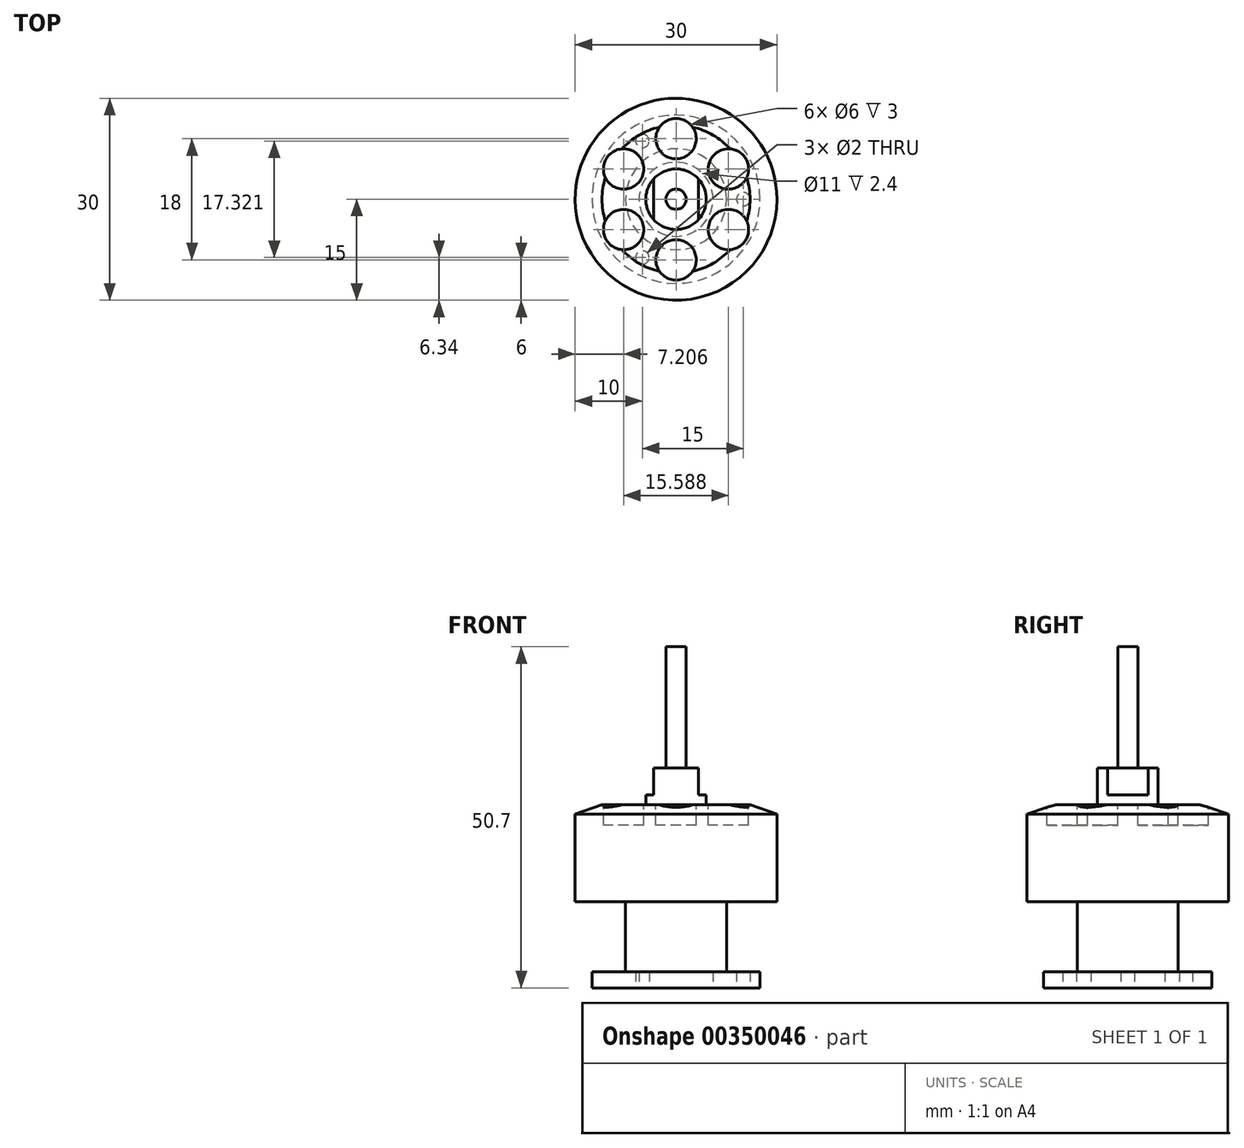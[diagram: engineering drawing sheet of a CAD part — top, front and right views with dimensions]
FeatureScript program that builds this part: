
annotation { "Feature Type Name" : "Feature", "Feature Type Description" : "" }
export const myFeature = defineFeature(function(context is Context, id is Id, definition is map)
    precondition{}
    {
        {
            var Q0;
            Q0=qCreatedBy(makeId("Top.planeOp"),FACE);
            var sketch = newSketch(context, id + "F0", { "sketchPlane" : qUnion([Q0])});
            skCircle(sketch, "E0", {"center": v(0, 0) * mm, "radius": 15 * mm});
            skSolve(sketch);
        }
        {
            var Q0;
            Q0=qSketchRegion(id+"F0",true);
            extrude(context, id + "F1", {"entities" : qUnion([Q0]), "depth" : 12 * mm});
        }
        {
            var Q0;
            Q0=qCreatedBy(makeId("Front.planeOp"),FACE);
            var sketch = newSketch(context, id + "F2", { "sketchPlane" : qUnion([Q0])});
            skLineSegment(sketch, "E1", {"start": v(0, 14.4) * mm, "end": v(0, 12) * mm});
            skLineSegment(sketch, "E2", {"start": v(0, 12) * mm, "end": v(15, 12) * mm});
            skLineSegment(sketch, "E3", {"start": v(11, 14.4) * mm, "end": v(0, 14.4) * mm});
            skLineSegment(sketch, "E4", {"start": v(11, 14.4) * mm, "end": v(15, 13) * mm});
            skLineSegment(sketch, "E5", {"start": v(15, 13) * mm, "end": v(15, 12) * mm});
            skSolve(sketch);
        }
        {
            var Q0;
            Q0=makeQuery(id+"F2.imprint","IMPRINT",FACE,{"disambiguationData":[TD([[makeQuery(id+"F2.imprint","IMPRINT",EDGE,{"derivedFrom":sQuery(id+"F2.wireOp",EDGE,"E1")}),1.0]])]});
            var Q1;
            Q1=sQuery(id+"F2.wireOp",EDGE,"E1");
            revolve(context, id + "F3", {"operationType" : NewBodyOperationType.ADD, "entities" : qUnion([Q0]), "axis" : qUnion([Q1]), "revolveType" : RevolveType.FULL});
        }
        {
            var Q0;
            Q0=makeQuery(id+"F3.opRevolve","SWEPT_FACE",FACE,{"disambiguationData":[OSD([sQuery(id+"F2.wireOp",EDGE,"E3")])]});
            var sketch = newSketch(context, id + "F4", { "sketchPlane" : qUnion([Q0])});
            skCircle(sketch, "E6", {"center": v(0, 9) * mm, "radius": 3 * mm});
            skCircle(sketch, "E7.1.0", {"center": v(-7.8, 4.5) * mm, "radius": 3 * mm});
            skCircle(sketch, "E7.2.0", {"center": v(-7.8, -4.5) * mm, "radius": 3 * mm});
            skCircle(sketch, "E7.3.0", {"center": v(0, -9) * mm, "radius": 3 * mm});
            skCircle(sketch, "E7.4.0", {"center": v(7.8, -4.5) * mm, "radius": 3 * mm});
            skCircle(sketch, "E7.5.0", {"center": v(7.8, 4.5) * mm, "radius": 3 * mm});
            skPoint(sketch, "E7.center", {"position": v(0, 0) * mm});
            skSolve(sketch);
        }
        {
            var Q0;
            Q0=qSketchRegion(id+"F4",true);
            extrude(context, id + "F5", {"entities" : qUnion([Q0]), "operationType" : NewBodyOperationType.REMOVE, "oppositeDirection" : true, "depth" : 3 * mm});
        }
        {
            var Q0;
            Q0=makeQuery(id+"F3.opRevolve","SWEPT_FACE",FACE,{"disambiguationData":[OSD([sQuery(id+"F2.wireOp",EDGE,"E3")])]});
            var sketch = newSketch(context, id + "F6", { "sketchPlane" : qUnion([Q0])});
            skCircle(sketch, "E8", {"center": v(0, 0) * mm, "radius": 4.5 * mm});
            skSolve(sketch);
        }
        {
            var Q0;
            Q0=qSketchRegion(id+"F6",true);
            extrude(context, id + "F7", {"entities" : qUnion([Q0]), "operationType" : NewBodyOperationType.ADD, "depth" : 1.5 * mm});
        }
        {
            var Q0;
            Q0=makeQuery(id+"F7.opExtrude","CAP_FACE",FACE,{"disambiguationData":[OSD([sQuery(id+"F6.wireOp",EDGE,"E8")])],"isStart":false});
            var sketch = newSketch(context, id + "F8", { "sketchPlane" : qUnion([Q0])});
            skCircle(sketch, "E9", {"center": v(0, 0) * mm, "radius": 4.5 * mm});
            skLineSegment(sketch, "E10", {"start": v(3.35, 3) * mm, "end": v(3.35, -3) * mm});
            skLineSegment(sketch, "E11", {"start": v(-3.35, 3) * mm, "end": v(-3.35, -3) * mm});
            skSolve(sketch);
        }
        {
            var Q0;
            {var subQ0=sQuery(id+"F8.wireOp",EDGE,"E10");Q0=makeQuery(id+"F8.imprint","IMPRINT",FACE,{"disambiguationData":[TD([[makeQuery(id+"F8.imprint","IMPRINT",EDGE,{"derivedFrom":subQ0}),-1.0]])]});}
            extrude(context, id + "F9", {"entities" : qUnion([Q0]), "operationType" : NewBodyOperationType.ADD, "depth" : 4 * mm});
        }
        {
            var Q0;
            Q0=makeQuery(id+"F9.opExtrude","CAP_FACE",FACE,{"disambiguationData":[OSD([sQuery(id+"F8.wireOp",EDGE,"E9"),sQuery(id+"F8.wireOp",EDGE,"E10"),sQuery(id+"F8.wireOp",EDGE,"E11")])],"isStart":false});
            var sketch = newSketch(context, id + "F10", { "sketchPlane" : qUnion([Q0])});
            skCircle(sketch, "E12", {"center": v(0, 0) * mm, "radius": 1.5 * mm});
            skSolve(sketch);
        }
        {
            var Q0;
            Q0=qSketchRegion(id+"F10",true);
            extrude(context, id + "F11", {"entities" : qUnion([Q0]), "operationType" : NewBodyOperationType.ADD, "depth" : 18 * mm});
        }
        {
            var Q0;
            Q0=makeQuery(id+"F1.opExtrude","CAP_FACE",FACE,{"disambiguationData":[OSD([sQuery(id+"F0.wireOp",EDGE,"E0")])],"isStart":true});
            var sketch = newSketch(context, id + "F12", { "sketchPlane" : qUnion([Q0])});
            skCircle(sketch, "E13", {"center": v(0, 0) * mm, "radius": 7.5 * mm});
            skSolve(sketch);
        }
        {
            var Q0;
            Q0=qSketchRegion(id+"F12",true);
            extrude(context, id + "F13", {"entities" : qUnion([Q0]), "operationType" : NewBodyOperationType.ADD, "depth" : 10.4 * mm});
        }
        {
            var Q0;
            Q0=makeQuery(id+"F13.opExtrude","CAP_FACE",FACE,{"disambiguationData":[OSD([sQuery(id+"F12.wireOp",EDGE,"E13")])],"isStart":false});
            var sketch = newSketch(context, id + "F14", { "sketchPlane" : qUnion([Q0])});
            skCircle(sketch, "E14", {"center": v(0, 0) * mm, "radius": 12.5 * mm});
            skSolve(sketch);
        }
        {
            var Q0;
            Q0=qSketchRegion(id+"F14",true);
            extrude(context, id + "F15", {"entities" : qUnion([Q0]), "operationType" : NewBodyOperationType.ADD, "depth" : 2.4 * mm});
        }
        {
            var Q0;
            Q0=makeQuery(id+"F15.opExtrude","CAP_FACE",FACE,{"disambiguationData":[OSD([sQuery(id+"F14.wireOp",EDGE,"E14")])],"isStart":false});
            var sketch = newSketch(context, id + "F16", { "sketchPlane" : qUnion([Q0])});
            skCircle(sketch, "E15", {"center": v(0, 0) * mm, "radius": 5.5 * mm});
            skCircle(sketch, "E16", {"center": v(0, 0) * mm, "radius": 10 * mm, "construction": true});
            skCircle(sketch, "E17", {"center": v(10, 0) * mm, "radius": 1 * mm});
            skCircle(sketch, "E18.1.0", {"center": v(-5, 8.66) * mm, "radius": 1 * mm});
            skCircle(sketch, "E18.2.0", {"center": v(-5, -8.66) * mm, "radius": 1 * mm});
            skSolve(sketch);
        }
        {
            var Q0;
            Q0=qSketchRegion(id+"F16",true);
            extrude(context, id + "F17", {"entities" : qUnion([Q0]), "operationType" : NewBodyOperationType.REMOVE, "oppositeDirection" : true, "depth" : 2.4 * mm});
        }
    });
